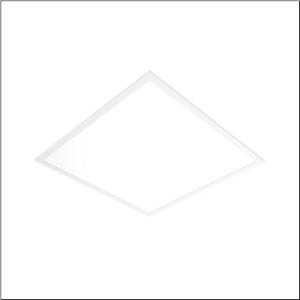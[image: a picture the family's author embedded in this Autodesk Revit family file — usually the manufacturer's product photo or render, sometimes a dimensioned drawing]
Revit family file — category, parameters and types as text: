
# Revit family: apollon_r__41_51mh12w72443_3f91
name_source: partatom
category: Lighting Fixtures
units: mm (PartAtom-declared; Revit-internal decimal feet)

## family parameters
Cut with Voids When Loaded = No
Host = Face
Light Source = No
Part Type = Normal
Room Calculation Point = No
Round Connector Dimension = Use Diameter
Shared = No

## types (1)
- Apollon® 41 (1 x LED, 3700 lm, 28.5 W, 4000K)
    Apparent Load = 29 VA
    CIE Flux Codes = 61 87 97 100 100
    Color Rendering = 80
    Color Temperature = 4000K
    Default Elevation = 1800 mm
    Description = Apollon® 41, office luminaire, primary optical cover: prismatic diffuser, of PS, light emission: direct distribution, primary light characteristic: symmetric, installation type: lay-in mounting, LED, rated luminous flux: 3.700lm, luminous efficacy: 130lm/W, light colour: 840, colour temperature: 4000K, with terminal, 3-pole, mains connection: 220..240V, AC, 50/60Hz, housing, of aluminium section, traffic white (RAL 9016), module: M600, length: 600mm, width: 600mm, height: 28mm, housing upper side, of sheet steel, protection rating (complete): IP20, protection rating (lamp compartment, on room side): IP40, insulation class (complete): insulation class II (safety insulation), certification: CE, ENEC, permissible operating ambient temperature: -25..+40°C, packaging unit: 1 piece
    Height = 0 mm  [stored 0 ft]
    Lamp = 1 x LED
    Lamp Light Flux = 3700 lm
    Lamp Power = 28.5 W
    Lamp count = 1
    Length = 600 mm
    Luminous efficacy = 130 lm/W
    Manufacturer = Siteco
    ModVariant = No
    Model = 51MH12W72443
    Mounting Place = Ceiling
    Mounting Type = Recessed
    Number of Poles = 1
    OnlyDefault = Yes
    Power Factor = 1
    Product Name = Apollon® 41
    Product group = office luminaire | ceiling recessed
    ProductGroupID = 401
    Protection Class = Protection class II
    Protection Degree = IP 20
    RLX_Detail_Level = 1
    RLX_Emergency_Light_Flux = 0 lm
    RLX_Emergency_Type = 0
    RLX_Emergency_Type_DB = No
    RlxData = <blob elided: 12185 chars, md5=6040831b>
    Socket = socket
    Standby Power = 0 W
    System Light Flux = 3700 lm
    System Power = 29 W
    Type Comments = Product without accessories
    Type Image = l_1291024.jpg
    URL = http://relux.com
    VarID = ---
    Voltage = 0 V
    Weight = 0.00 kg
    Width = 600 mm

note: [stored X ft] marks values corroborated as IEEE doubles in the binary element streams (Revit-internal decimal feet)

## geometry (parser evidence)
native form markers: Sweep x10
no freeform markers — native parametric forms only
